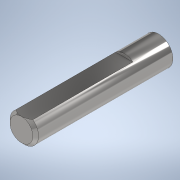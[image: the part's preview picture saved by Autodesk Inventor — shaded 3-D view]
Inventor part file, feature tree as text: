
AUTODESK INVENTOR PART (.ipt)
format: ipt  version: 2022 (Build 260153000, 153)  size: 116,224 bytes
history: native  units: mm
features: extrude x2, sketch x2, chamfer x1
ambient origin geometry x8: Origin, YZ Plane, XZ Plane, XY Plane, X Axis, Y Axis, Z Axis, Center Point
bodies: Solid1 (feature_tree)
feature tree (5):
  extrude  "Extrusion1"  Depth=24.0mm TaperAngle=0.0deg
  extrude  "Extrusion2"  Depth=2.5mm TaperAngle=0.0deg
  chamfer  "Chamfer1"  Distance=0.5mm Angle=45.0deg
  sketch  "Sketch1"  dims[d0=5.0mm d1=24.0mm d2=0.0mm]
  sketch  "Sketch2"  dims[d3=2.5mm d4=6.0mm d5=0.0mm d6=0.5mm d7=2.0mm d8=45.0deg]
